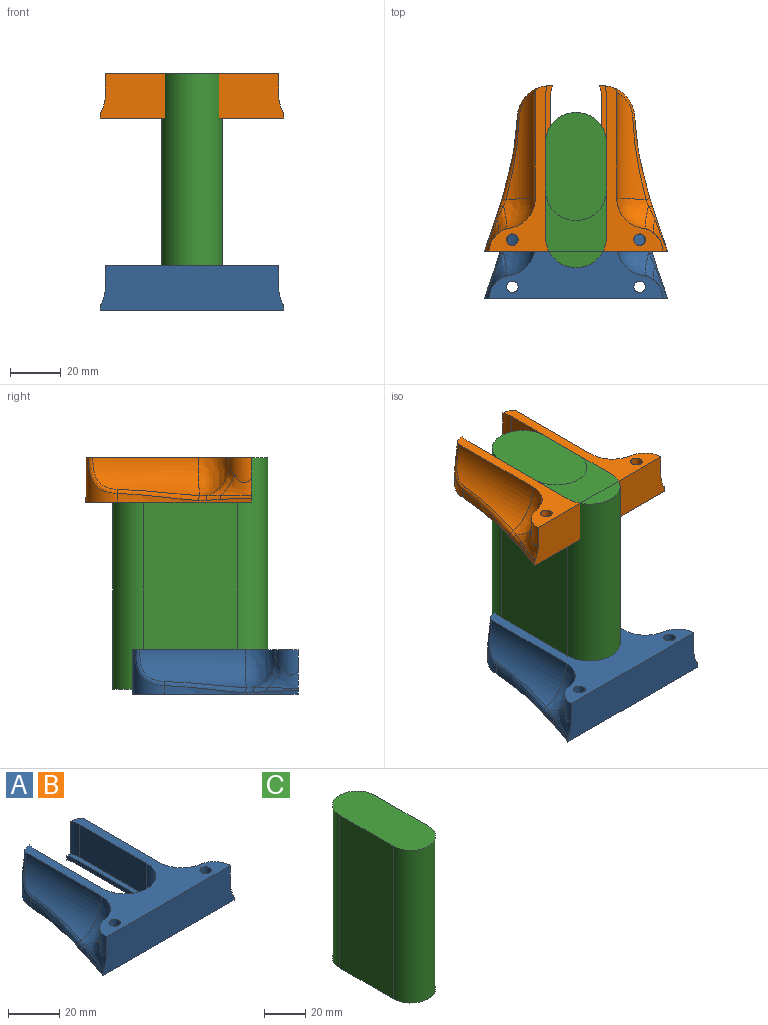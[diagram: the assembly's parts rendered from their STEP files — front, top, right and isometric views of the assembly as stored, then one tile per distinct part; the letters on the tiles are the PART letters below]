
ASSEMBLY  parts=3 mates=2
PART A: 42 faces, bbox 76.1x70.3x20.3 mm
  f0: cylinder r=15.5mm len=42.04mm, axis (0,-1,0), area 627.2mm2, adj f3,f16,f19,f20
  f1: plane 53x24mm, normal (0,0,1), area 233.4mm2, adj f4,f5,f7,f9,f10,f11,f12,f13
  f2: extruded ~52.65x12.94mm, area 89.8mm2, adj f6,f8,f13,f20,f21,f22,f23
  f3: plane 68.29x65.23mm, normal (0,0,1), area 1180.3mm2, adj f0,f5,f6,f9,f11,f13,f14,f15
  f4: cylinder r=10mm len=4mm, axis (0,0,1), area 8.2mm2, adj f1,f7,f8,f12
  f5: cylinder r=12mm len=15.5mm, axis (0,0,1), area 62.2mm2, adj f1,f3,f9,f13
  f6: plane 73.28x18.78mm, normal (0,-1,0), area 1207.2mm2, adj f2,f3,f8,f14,f18,f23,f25,f32
  f7: plane 37x2mm, normal (1,0,0), area 74mm2, adj f1,f4,f8,f10
  f8: plane 72x65mm, normal (0,0,-1), area 2451.4mm2, adj f2,f4,f6,f7,f10,f12,f13,f15
  f9: plane 37x15.5mm, normal (1,0,0), area 573.5mm2, adj f1,f3,f5,f11
  f10: cylinder r=10mm len=20mm, axis (0,0,1), area 62.8mm2, adj f1,f7,f8,f28
  f11: cylinder r=12mm len=24mm, axis (0,0,1), area 584.3mm2, adj f1,f3,f9,f29
  f12: plane 2x0.91mm, normal (0,1,0), area 1.8mm2, adj f1,f4,f8,f13
  f13: cylinder r=13mm len=17.5mm, axis (0,0,-1), area 159.8mm2, adj f1,f2,f3,f5,f8,f12,f19
  f14: cylinder r=9mm len=9.94mm, axis (0,0,-1), area 89.4mm2, adj f3,f6,f16,f17,f18
  f15: cylinder r=2.25mm len=17.5mm, axis (0,0,1), area 247.4mm2, adj f3,f8
  f16: bspline ~17x14.2mm, area 249.6mm2, adj f0,f3,f14,f17,f21
  f17: bspline ~14.48x12.16mm, area 53.6mm2, adj f14,f16,f18,f22
  f18: bspline ~17.38x9.09mm, area 71.2mm2, adj f6,f14,f17,f23
  f19: bspline ~15.25x13.84mm, area 44mm2, adj f0,f3,f13,f20
  f20: bspline ~43.82x8.65mm, area 71.5mm2, adj f0,f2,f19,f21
  f21: bspline ~6.52x3.31mm, area 8mm2, adj f2,f16,f20,f22
  f22: bspline ~6.29x3.51mm, area 11.3mm2, adj f2,f17,f21,f23
  f23: bspline ~15.37x5.96mm, area 13.8mm2, adj f2,f6,f18,f22
  f24: cylinder r=15.5mm len=42.04mm, axis (0,-1,0), area 627.2mm2, adj f3,f34,f37,f38
  f25: extruded ~52.65x12.94mm, area 89.8mm2, adj f6,f8,f31,f38,f39,f40,f41
  f26: cylinder r=10mm len=4mm, axis (0,0,1), area 8.2mm2, adj f1,f8,f28,f30
  f27: cylinder r=12mm len=15.5mm, axis (0,0,1), area 62.2mm2, adj f1,f3,f29,f31
  f28: plane 37x2mm, normal (-1,0,0), area 74mm2, adj f1,f8,f10,f26
  f29: plane 37x15.5mm, normal (-1,0,0), area 573.5mm2, adj f1,f3,f11,f27
  f30: plane 2x0.91mm, normal (0,1,0), area 1.8mm2, adj f1,f8,f26,f31
  f31: cylinder r=13mm len=17.5mm, axis (0,0,-1), area 159.8mm2, adj f1,f3,f8,f25,f27,f30,f37
  f32: cylinder r=9mm len=9.94mm, axis (0,0,-1), area 89.4mm2, adj f3,f6,f34,f35,f36
  f33: cylinder r=2.25mm len=17.5mm, axis (0,0,1), area 247.4mm2, adj f3,f8
  f34: bspline ~17x14.2mm, area 249.6mm2, adj f3,f24,f32,f35,f39
  f35: bspline ~14.48x12.16mm, area 53.6mm2, adj f32,f34,f36,f40
  f36: bspline ~17.38x9.09mm, area 71.2mm2, adj f6,f32,f35,f41
  f37: bspline ~15.25x12.68mm, area 44mm2, adj f3,f24,f31,f38
  f38: bspline ~43.82x8.65mm, area 71.5mm2, adj f24,f25,f37,f39
  f39: bspline ~6.52x3.31mm, area 8mm2, adj f25,f34,f38,f40
  f40: bspline ~6.29x3.51mm, area 11.3mm2, adj f25,f35,f39,f41
  f41: bspline ~15.37x5.96mm, area 13.8mm2, adj f6,f25,f36,f40
PART B: same geometry as A
PART C: 6 faces, bbox 24x61x91 mm
  f0: cylinder r=12mm len=91mm, axis (0,0,-1), area 3430.6mm2, adj f1,f2,f3,f4
  f1: plane 91x37mm, normal (-1,0,0), area 3367mm2, adj f0,f2,f3,f5
  f2: plane 61x24mm, normal (0,0,1), area 1340.4mm2, adj f0,f1,f4,f5
  f3: plane 61x24mm, normal (0,0,-1), area 1340.4mm2, adj f0,f1,f4,f5
  f4: plane 91x37mm, normal (1,0,0), area 3367mm2, adj f0,f2,f3,f5
  f5: cylinder r=12mm len=91mm, axis (0,0,-1), area 3430.6mm2, adj f1,f2,f3,f4
PLACE A rot(axis=(-0.22,0.96,0.16),0deg) t=(-1.79,-17.91,61.53)mm
PLACE B rot(axis=(-0.22,0.96,0.16),0deg) t=(-1.79,0.47,137.03)mm
PLACE C rot(axis=(-0.22,0.96,0.16),0deg) t=(-1.79,24.47,63.53)mm
MATE fastened B.f11 <-> C.f2  axis (0,0,1) through (-1.79,24.47,154.53)mm
MATE fastened A.f1 <-> C.f3  axis (0,0,1) through (-1.79,24.47,63.53)mm
